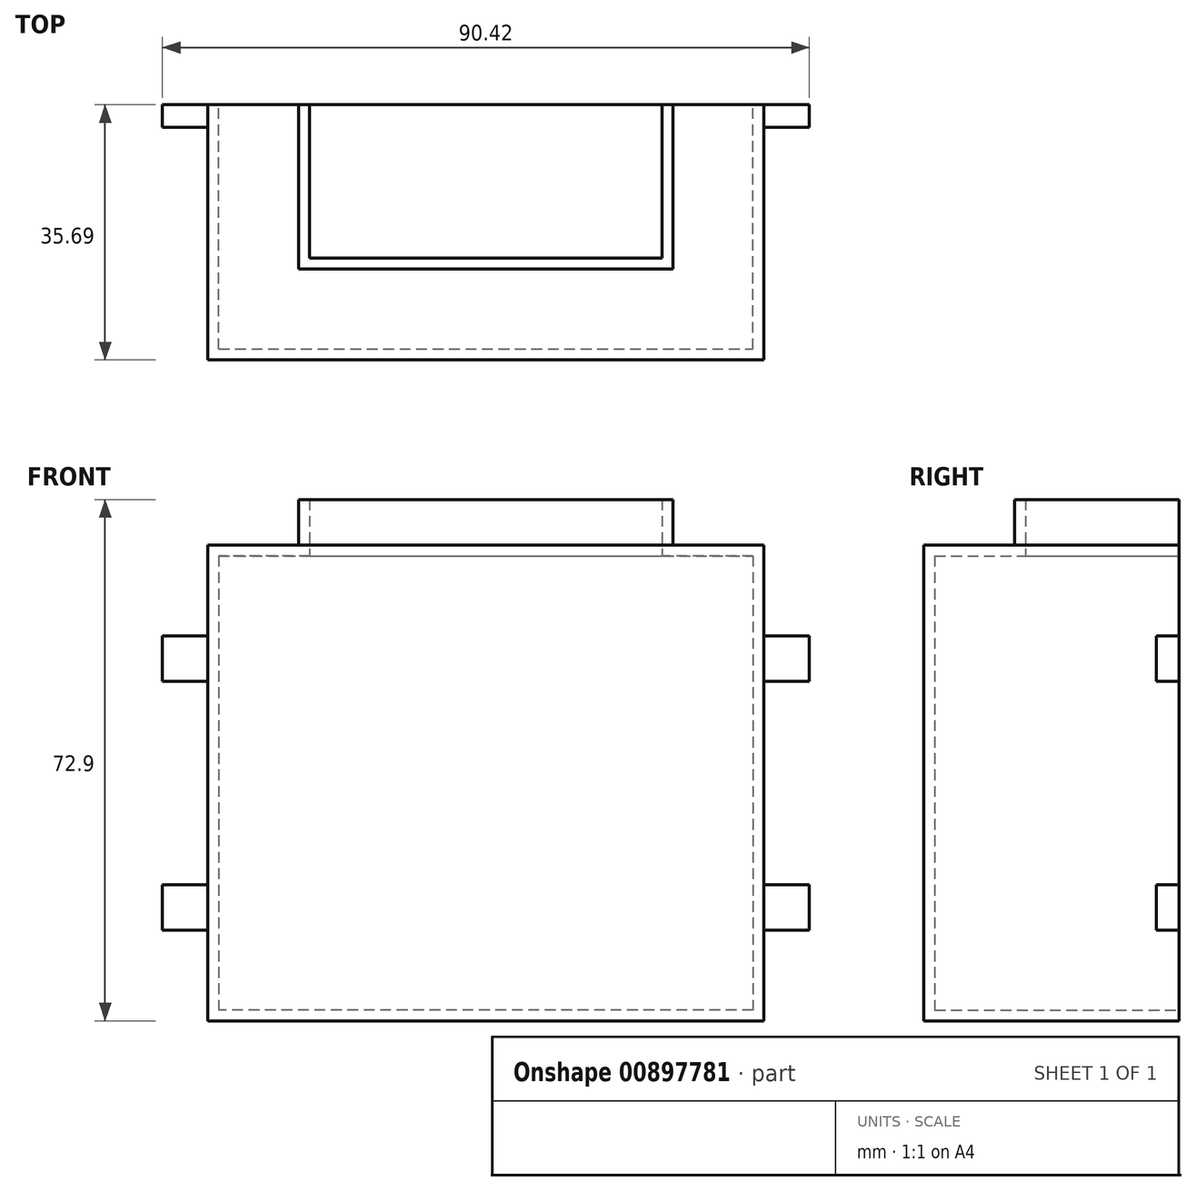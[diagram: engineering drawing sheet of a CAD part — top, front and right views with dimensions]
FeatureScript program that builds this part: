
annotation { "Feature Type Name" : "Feature", "Feature Type Description" : "" }
export const myFeature = defineFeature(function(context is Context, id is Id, definition is map)
    precondition{}
    {
        {
            var Q0;
            Q0=qCreatedBy(makeId("Top.planeOp"),FACE);
            var sketch = newSketch(context, id + "F0", { "sketchPlane" : qUnion([Q0])});
            skLineSegment(sketch, "E0.bottom", {"start": v(0, 0) * mm, "end": v(77.72, 0) * mm});
            skLineSegment(sketch, "E0.top", {"start": v(0, 35.69) * mm, "end": v(77.72, 35.69) * mm});
            skLineSegment(sketch, "E0.left", {"start": v(0, 0) * mm, "end": v(0, 35.69) * mm});
            skLineSegment(sketch, "E0.right", {"start": v(77.72, 0) * mm, "end": v(77.72, 35.69) * mm});
            skSolve(sketch);
        }
        {
            var Q0;
            Q0 = qSketchRegion(id + "F0", true);
            extrude(context, id + "F1", {"entities" : qUnion([Q0]), "depth" : 66.55 * mm, "offsetDistance" : 25.4 * mm});
        }
        {
            var Q0;
            Q0=makeQuery(id+"F1.opExtrude","CAP_FACE",FACE,{"disambiguationData":[OSD([sQuery(id+"F0.wireOp",EDGE,"E0.bottom"),sQuery(id+"F0.wireOp",EDGE,"E0.top"),sQuery(id+"F0.wireOp",EDGE,"E0.left"),sQuery(id+"F0.wireOp",EDGE,"E0.right")])],"isStart":false});
            var Q1;
            Q1=makeQuery(id+"F1.opExtrude","SWEPT_BODY",BODY,{"disambiguationData":[OSD([sQuery(id+"F0.wireOp",EDGE,"E0.bottom"),sQuery(id+"F0.wireOp",EDGE,"E0.top"),sQuery(id+"F0.wireOp",EDGE,"E0.left"),sQuery(id+"F0.wireOp",EDGE,"E0.right")])]});
            shell(context, id + "F2", {"isHollow" : true, "entities" : qUnion([Q0]), "parts" : qUnion([Q1]), "thickness" : 1.52 * mm});
        }
        {
            var Q0;
            Q0=makeQuery(id+"F1.opExtrude","CAP_FACE",FACE,{"disambiguationData":[OSD([sQuery(id+"F0.wireOp",EDGE,"E0.bottom"),sQuery(id+"F0.wireOp",EDGE,"E0.top"),sQuery(id+"F0.wireOp",EDGE,"E0.left"),sQuery(id+"F0.wireOp",EDGE,"E0.right")])],"isStart":false});
            var sketch = newSketch(context, id + "F3", { "sketchPlane" : qUnion([Q0])});
            skLineSegment(sketch, "E1.bottom", {"start": v(14.22, 14.22) * mm, "end": v(63.5, 14.22) * mm});
            skLineSegment(sketch, "E1.left", {"start": v(14.22, 14.22) * mm, "end": v(14.22, 35.69) * mm});
            skLineSegment(sketch, "E1.right", {"start": v(63.5, 14.22) * mm, "end": v(63.5, 35.69) * mm});
            skLineSegment(sketch, "E2.bottom", {"start": v(12.7, 12.7) * mm, "end": v(65.02, 12.7) * mm});
            skLineSegment(sketch, "E2.left", {"start": v(12.7, 12.7) * mm, "end": v(12.7, 35.69) * mm});
            skLineSegment(sketch, "E2.right", {"start": v(65.02, 12.7) * mm, "end": v(65.02, 35.69) * mm});
            skSolve(sketch);
        }
        {
            var Q0;
            Q0 = qSketchRegion(id + "F3", true);
            var Q1;
            Q1=makeQuery(id+"F3.imprint","IMPRINT",FACE,{"disambiguationData":[TD([[makeQuery(id+"F3.imprint","IMPRINT",EDGE,{"derivedFrom":sQuery(id+"F3.wireOp",EDGE,"E1.bottom")}),-1.0]])]});
            extrude(context, id + "F4", {"entities" : qUnion([Q0, Q1]), "operationType" : NewBodyOperationType.ADD, "depth" : 6.35 * mm, "offsetDistance" : 25.4 * mm});
        }
        {
            var Q0;
            Q0=makeQuery(id+"F4.boolean.opBoolean","SPLIT",FACE,{"disambiguationData":[TD([makeQuery(id+"F4.opExtrude","SWEPT_FACE",FACE,{"disambiguationData":[OSD([sQuery(id+"F3.wireOp",EDGE,"E1.bottom")])]})])],"derivedFrom":makeQuery(id+"F1.opExtrude","CAP_FACE",FACE,{"disambiguationData":[OSD([sQuery(id+"F0.wireOp",EDGE,"E0.bottom"),sQuery(id+"F0.wireOp",EDGE,"E0.top"),sQuery(id+"F0.wireOp",EDGE,"E0.left"),sQuery(id+"F0.wireOp",EDGE,"E0.right")])],"isStart":false})});
            extrude(context, id + "F5", {"entities" : qUnion([Q0]), "operationType" : NewBodyOperationType.REMOVE, "oppositeDirection" : true, "depth" : 25.4 * mm, "offsetDistance" : 25.4 * mm});
        }
        {
            var Q0;
            Q0=makeQuery(id+"F1.opExtrude","SWEPT_FACE",FACE,{"disambiguationData":[OSD([sQuery(id+"F0.wireOp",EDGE,"E0.right")])]});
            var sketch = newSketch(context, id + "F6", { "sketchPlane" : qUnion([Q0])});
            skLineSegment(sketch, "E3.bottom", {"start": v(32.51, 19.05) * mm, "end": v(35.69, 19.05) * mm});
            skLineSegment(sketch, "E3.top", {"start": v(32.51, 12.7) * mm, "end": v(35.69, 12.7) * mm});
            skLineSegment(sketch, "E3.left", {"start": v(32.51, 19.05) * mm, "end": v(32.51, 12.7) * mm});
            skLineSegment(sketch, "E3.right", {"start": v(35.69, 19.05) * mm, "end": v(35.69, 12.7) * mm});
            skLineSegment(sketch, "E4.bottom", {"start": v(32.51, 53.85) * mm, "end": v(35.69, 53.85) * mm});
            skLineSegment(sketch, "E4.top", {"start": v(32.51, 47.5) * mm, "end": v(35.69, 47.5) * mm});
            skLineSegment(sketch, "E4.left", {"start": v(32.51, 53.85) * mm, "end": v(32.51, 47.5) * mm});
            skLineSegment(sketch, "E4.right", {"start": v(35.69, 53.85) * mm, "end": v(35.69, 47.5) * mm});
            skSolve(sketch);
        }
        {
            var Q0;
            Q0 = qSketchRegion(id + "F6", true);
            extrude(context, id + "F7", {"entities" : qUnion([Q0]), "operationType" : NewBodyOperationType.ADD, "depth" : 6.35 * mm, "offsetDistance" : 25.4 * mm});
        }
        {
            var Q0;
            Q0=makeQuery(id+"F1.opExtrude","SWEPT_FACE",FACE,{"disambiguationData":[OSD([sQuery(id+"F0.wireOp",EDGE,"E0.left")])]});
            var sketch = newSketch(context, id + "F8", { "sketchPlane" : qUnion([Q0])});
            skLineSegment(sketch, "E5.bottom", {"start": v(-35.69, 19.05) * mm, "end": v(-32.51, 19.05) * mm});
            skLineSegment(sketch, "E5.top", {"start": v(-35.69, 12.7) * mm, "end": v(-32.51, 12.7) * mm});
            skLineSegment(sketch, "E5.left", {"start": v(-35.69, 19.05) * mm, "end": v(-35.69, 12.7) * mm});
            skLineSegment(sketch, "E5.right", {"start": v(-32.51, 19.05) * mm, "end": v(-32.51, 12.7) * mm});
            skLineSegment(sketch, "E6.bottom", {"start": v(-35.69, 53.85) * mm, "end": v(-32.51, 53.85) * mm});
            skLineSegment(sketch, "E6.top", {"start": v(-35.69, 47.5) * mm, "end": v(-32.51, 47.5) * mm});
            skLineSegment(sketch, "E6.left", {"start": v(-35.69, 53.85) * mm, "end": v(-35.69, 47.5) * mm});
            skLineSegment(sketch, "E6.right", {"start": v(-32.51, 53.85) * mm, "end": v(-32.51, 47.5) * mm});
            skSolve(sketch);
        }
        {
            var Q0;
            Q0 = qSketchRegion(id + "F8", true);
            extrude(context, id + "F9", {"entities" : qUnion([Q0]), "operationType" : NewBodyOperationType.ADD, "depth" : 6.35 * mm, "offsetDistance" : 25.4 * mm});
        }
        {
            var Q0;
            {var subQ0=sQuery(id+"F0.wireOp",EDGE,"E0.top");var subQ1=makeQuery(id+"F1.opExtrude","CAP_EDGE",EDGE,{"disambiguationData":[OSD([subQ0])],"isStart":false});Q0=makeQuery(id+"F9.boolean.opBoolean","MERGE",FACE,{"derivedFrom":[makeQuery(id+"F7.boolean.opBoolean","MERGE",FACE,{"derivedFrom":[makeQuery(id+"F4.boolean.opBoolean","MERGE",FACE,{"derivedFrom":[makeQuery(id+"F1.opExtrude","SWEPT_FACE",FACE,{"disambiguationData":[OSD([subQ0])]}),makeQuery(id+"F4.opExtrude","SWEPT_FACE",FACE,{"disambiguationData":[OSD([subQ0]),TDD([makeQuery(id+"F3.imprint","IMPRINT",EDGE,{"disambiguationData":[TD([[makeQuery(id+"F3.imprint","INTERSECT",VERTEX,{"derivedFrom":[subQ1,sQuery(id+"F3.wireOp",EDGE,"E1.left")]}),1.0]])],"derivedFrom":subQ1})])]}),makeQuery(id+"F4.opExtrude","SWEPT_FACE",FACE,{"disambiguationData":[OSD([subQ0]),TDD([makeQuery(id+"F3.imprint","IMPRINT",EDGE,{"disambiguationData":[TD([[makeQuery(id+"F3.imprint","INTERSECT",VERTEX,{"derivedFrom":[subQ1,sQuery(id+"F3.wireOp",EDGE,"E1.right")]}),-1.0]])],"derivedFrom":subQ1})])]})]}),makeQuery(id+"F7.opExtrude","SWEPT_FACE",FACE,{"disambiguationData":[OSD([sQuery(id+"F6.wireOp",EDGE,"E3.right")])]}),makeQuery(id+"F7.opExtrude","SWEPT_FACE",FACE,{"disambiguationData":[OSD([sQuery(id+"F6.wireOp",EDGE,"E4.right")])]})]}),makeQuery(id+"F9.opExtrude","SWEPT_FACE",FACE,{"disambiguationData":[OSD([sQuery(id+"F8.wireOp",EDGE,"E5.left")])]}),makeQuery(id+"F9.opExtrude","SWEPT_FACE",FACE,{"disambiguationData":[OSD([sQuery(id+"F8.wireOp",EDGE,"E6.left")])]})]});}
            var sketch = newSketch(context, id + "F10", { "sketchPlane" : qUnion([Q0])});
            skLineSegment(sketch, "E7.bottom", {"start": v(-76.2, 65.02) * mm, "end": v(-1.52, 65.02) * mm});
            skLineSegment(sketch, "E7.top", {"start": v(-76.2, 1.52) * mm, "end": v(-1.52, 1.52) * mm});
            skLineSegment(sketch, "E7.left", {"start": v(-76.2, 65.02) * mm, "end": v(-76.2, 1.52) * mm});
            skLineSegment(sketch, "E7.right", {"start": v(-1.52, 65.02) * mm, "end": v(-1.52, 1.52) * mm});
            skSolve(sketch);
        }
        {
            var Q0;
            Q0 = qSketchRegion(id + "F10", true);
            extrude(context, id + "F11", {"entities" : qUnion([Q0]), "operationType" : NewBodyOperationType.REMOVE, "oppositeDirection" : true, "depth" : 1.52 * mm, "offsetDistance" : 25.4 * mm});
        }
    });
